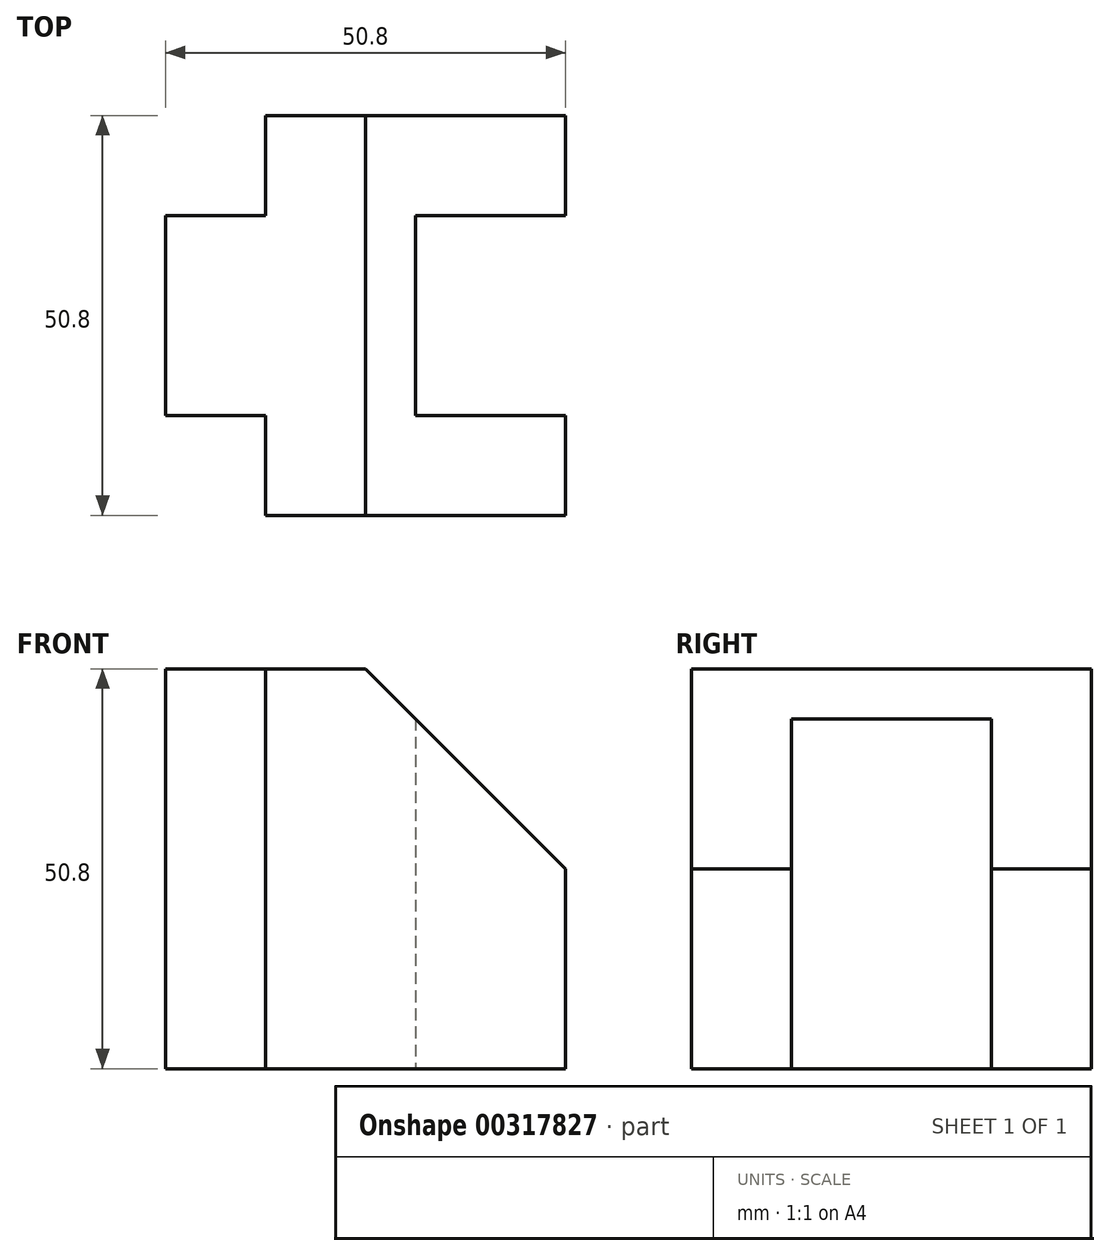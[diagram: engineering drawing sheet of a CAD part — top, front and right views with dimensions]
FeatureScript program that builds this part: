
annotation { "Feature Type Name" : "Feature", "Feature Type Description" : "" }
export const myFeature = defineFeature(function(context is Context, id is Id, definition is map)
    precondition{}
    {
        {
            var Q0;
            Q0=qCreatedBy(makeId("Front.planeOp"),FACE);
            var sketch = newSketch(context, id + "F0", { "sketchPlane" : qUnion([Q0])});
            skLineSegment(sketch, "E0", {"start": v(0, 0) * mm, "end": v(0, 50.8) * mm});
            skLineSegment(sketch, "E1", {"start": v(0, 50.8) * mm, "end": v(50.8, 50.8) * mm});
            skLineSegment(sketch, "E2", {"start": v(50.8, 50.8) * mm, "end": v(50.8, 0) * mm});
            skLineSegment(sketch, "E3", {"start": v(50.8, 0) * mm, "end": v(0, 0) * mm});
            skSolve(sketch);
        }
        {
            var Q0;
            Q0=makeQuery(id+"F0.imprint","IMPRINT",FACE,{"disambiguationData":[TD([[makeQuery(id+"F0.imprint","IMPRINT",EDGE,{"derivedFrom":sQuery(id+"F0.wireOp",EDGE,"E0")}),-1.0]])]});
            extrude(context, id + "F1", {"entities" : qUnion([Q0]), "endBound" : BoundingType.SYMMETRIC, "depth" : 50.8 * mm});
        }
        {
            var Q0;
            Q0=makeQuery(id+"F1.opExtrude","CAP_FACE",FACE,{"disambiguationData":[OSD([sQuery(id+"F0.wireOp",EDGE,"E0"),sQuery(id+"F0.wireOp",EDGE,"E1"),sQuery(id+"F0.wireOp",EDGE,"E2"),sQuery(id+"F0.wireOp",EDGE,"E3")])],"isStart":false});
            var sketch = newSketch(context, id + "F2", { "sketchPlane" : qUnion([Q0])});
            skLineSegment(sketch, "E4", {"start": v(0, 50.8) * mm, "end": v(0, 0) * mm});
            skLineSegment(sketch, "E5", {"start": v(0, 0) * mm, "end": v(50.8, 0) * mm});
            skLineSegment(sketch, "E6", {"start": v(50.8, 0) * mm, "end": v(50.8, 25.4) * mm});
            skLineSegment(sketch, "E7", {"start": v(0, 50.8) * mm, "end": v(25.4, 50.8) * mm});
            skLineSegment(sketch, "E8", {"start": v(25.4, 50.8) * mm, "end": v(50.8, 25.4) * mm});
            skSolve(sketch);
        }
        {
            var Q0;
            {var subQ0=sQuery(id+"F2.wireOp",EDGE,"E8");Q0=makeQuery(id+"F2.imprint","IMPRINT",FACE,{"disambiguationData":[TD([[makeQuery(id+"F2.imprint","IMPRINT",EDGE,{"derivedFrom":subQ0}),1.0]])]});}
            extrude(context, id + "F3", {"entities" : qUnion([Q0]), "operationType" : NewBodyOperationType.REMOVE, "endBound" : BoundingType.THROUGH_ALL, "oppositeDirection" : true, "depth" : 25.4 * mm});
        }
        {
            var Q0;
            Q0=makeQuery(id+"F1.opExtrude","SWEPT_FACE",FACE,{"disambiguationData":[OSD([sQuery(id+"F0.wireOp",EDGE,"E3")])]});
            var sketch = newSketch(context, id + "F4", { "sketchPlane" : qUnion([Q0])});
            skLineSegment(sketch, "E9", {"start": v(-6.61, 0) * mm, "end": v(59.95, 0) * mm, "construction": true});
            skPoint(sketch, "E9.endSnap0", {"position": v(50.8, 0) * mm});
            skLineSegment(sketch, "E10", {"start": v(0, 0) * mm, "end": v(0, -12.7) * mm});
            skLineSegment(sketch, "E11", {"start": v(0, -12.7) * mm, "end": v(12.7, -12.7) * mm});
            skLineSegment(sketch, "E12", {"start": v(12.7, -12.7) * mm, "end": v(12.7, -25.4) * mm});
            skLineSegment(sketch, "E13", {"start": v(12.7, -25.4) * mm, "end": v(50.8, -25.4) * mm});
            skLineSegment(sketch, "E14", {"start": v(50.8, -25.4) * mm, "end": v(50.8, -12.7) * mm});
            skLineSegment(sketch, "E15", {"start": v(50.8, -12.7) * mm, "end": v(31.75, -12.7) * mm});
            skLineSegment(sketch, "E16", {"start": v(31.75, -12.7) * mm, "end": v(31.75, 0) * mm});
            skLineSegment(sketch, "E17.MirrorCS", {"start": v(0, 0) * mm, "end": v(0, 12.7) * mm});
            skLineSegment(sketch, "E18.MirrorCS", {"start": v(0, 12.7) * mm, "end": v(12.7, 12.7) * mm});
            skLineSegment(sketch, "E19.MirrorCS", {"start": v(12.7, 12.7) * mm, "end": v(12.7, 25.4) * mm});
            skLineSegment(sketch, "E20.MirrorCS", {"start": v(12.7, 25.4) * mm, "end": v(50.8, 25.4) * mm});
            skLineSegment(sketch, "E21.MirrorCS", {"start": v(50.8, 25.4) * mm, "end": v(50.8, 12.7) * mm});
            skLineSegment(sketch, "E22.MirrorCS", {"start": v(50.8, 12.7) * mm, "end": v(31.75, 12.7) * mm});
            skLineSegment(sketch, "E23.MirrorCS", {"start": v(31.75, 12.7) * mm, "end": v(31.75, 0) * mm});
            skSolve(sketch);
        }
        {
            var Q0;
            {var subQ0=sQuery(id+"F4.wireOp",EDGE,"E18.MirrorCS");Q0=makeQuery(id+"F4.imprint","IMPRINT",FACE,{"disambiguationData":[TD([[makeQuery(id+"F4.imprint","IMPRINT",EDGE,{"derivedFrom":subQ0}),1.0]])]});}
            var Q1;
            {var subQ0=sQuery(id+"F4.wireOp",EDGE,"E11");Q1=makeQuery(id+"F4.imprint","IMPRINT",FACE,{"disambiguationData":[TD([[makeQuery(id+"F4.imprint","IMPRINT",EDGE,{"derivedFrom":subQ0}),-1.0]])]});}
            var Q2;
            {var subQ1=sQuery(id+"F4.wireOp",EDGE,"E15");Q2=makeQuery(id+"F4.imprint","IMPRINT",FACE,{"disambiguationData":[TD([[makeQuery(id+"F4.imprint","IMPRINT",EDGE,{"derivedFrom":subQ1}),-1.0]])]});}
            extrude(context, id + "F5", {"entities" : qUnion([Q0, Q1, Q2]), "operationType" : NewBodyOperationType.REMOVE, "endBound" : BoundingType.THROUGH_ALL, "oppositeDirection" : true, "depth" : 25.4 * mm});
        }
    });
